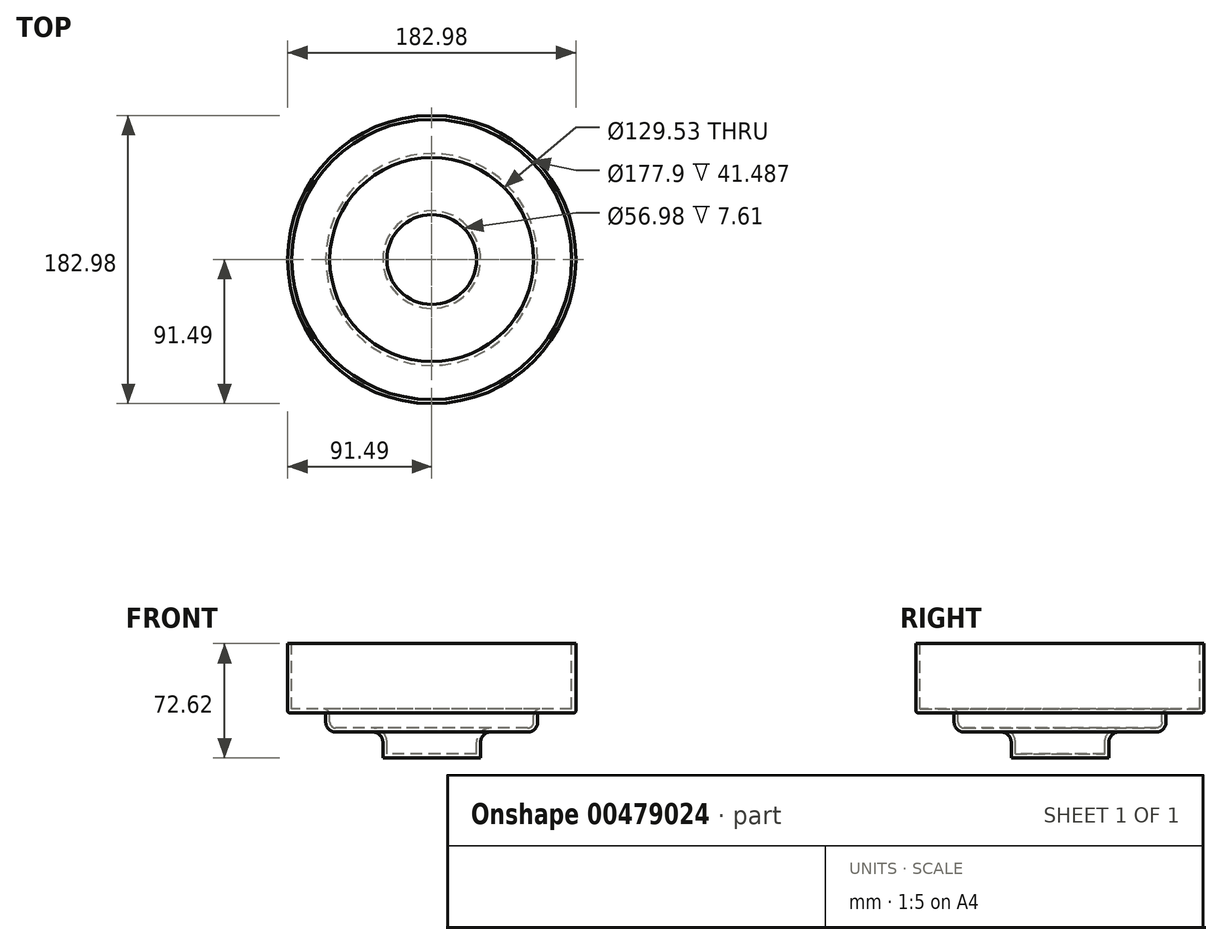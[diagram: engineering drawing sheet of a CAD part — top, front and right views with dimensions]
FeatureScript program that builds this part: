
annotation { "Feature Type Name" : "Feature", "Feature Type Description" : "" }
export const myFeature = defineFeature(function(context is Context, id is Id, definition is map)
    precondition{}
    {
        {
            var Q0;
            Q0=qCreatedBy(makeId("Front.planeOp"),FACE);
            var sketch = newSketch(context, id + "F0", { "sketchPlane" : qUnion([Q0])});
            skLineSegment(sketch, "E0", {"start": v(0, 0) * mm, "end": v(31.03, 0) * mm});
            skLineSegment(sketch, "E1", {"start": v(31.03, 0) * mm, "end": v(31.03, 10.15) * mm});
            skLineSegment(sketch, "E2", {"start": v(37.38, 16.5) * mm, "end": v(60.96, 16.5) * mm});
            skLineSegment(sketch, "E3", {"start": v(67.3, 22.85) * mm, "end": v(67.3, 27.2) * mm});
            skLineSegment(sketch, "E4", {"start": v(68.7, 28.6) * mm, "end": v(90.1, 28.6) * mm});
            skLineSegment(sketch, "E5", {"start": v(91.49, 29.98) * mm, "end": v(91.49, 72.62) * mm});
            skLineSegment(sketch, "E6", {"start": v(91.49, 72.62) * mm, "end": v(0, 72.62) * mm});
            skLineSegment(sketch, "E7", {"start": v(0, 72.62) * mm, "end": v(0, 0) * mm, "construction": true});
            skPoint(sketch, "E8.visualSharp", {"position": v(31.03, 16.5) * mm});
            skArc(sketch, "E8.filletArc", {"start": v(37.38, 16.5) * mm, "mid": v(32.9, 14.64) * mm, "end": v(31.03, 10.15) * mm});
            skPoint(sketch, "E9.visualSharp", {"position": v(67.3, 16.5) * mm});
            skArc(sketch, "E9.filletArc", {"start": v(60.96, 16.5) * mm, "mid": v(65.45, 18.36) * mm, "end": v(67.3, 22.85) * mm});
            skPoint(sketch, "E10.visualSharp", {"position": v(67.3, 28.6) * mm});
            skArc(sketch, "E10.filletArc", {"start": v(68.7, 28.6) * mm, "mid": v(67.71, 28.19) * mm, "end": v(67.3, 27.2) * mm});
            skPoint(sketch, "E11.visualSharp", {"position": v(91.49, 28.6) * mm});
            skArc(sketch, "E11.filletArc", {"start": v(90.1, 28.6) * mm, "mid": v(91.08, 29) * mm, "end": v(91.49, 29.98) * mm});
            skLineSegment(sketch, "E12", {"start": v(0, 72.62) * mm, "end": v(0, 0) * mm});
            skSolve(sketch);
        }
        {
            var Q0;
            Q0 = qSketchRegion(id + "F0", true);
            var Q1;
            Q1=sQuery(id+"F0.wireOp",EDGE,"E12");
            revolve(context, id + "F1", {"entities" : qUnion([Q0]), "axis" : qUnion([Q1]), "revolveType" : RevolveType.FULL});
        }
        {
            var Q0;
            Q0=makeQuery(id+"F1.opRevolve","SWEPT_FACE",FACE,{"disambiguationData":[OSD([sQuery(id+"F0.wireOp",EDGE,"E6")])]});
            shell(context, id + "F2", {"entities" : qUnion([Q0]), "thickness" : 2.54 * mm});
        }
    });
